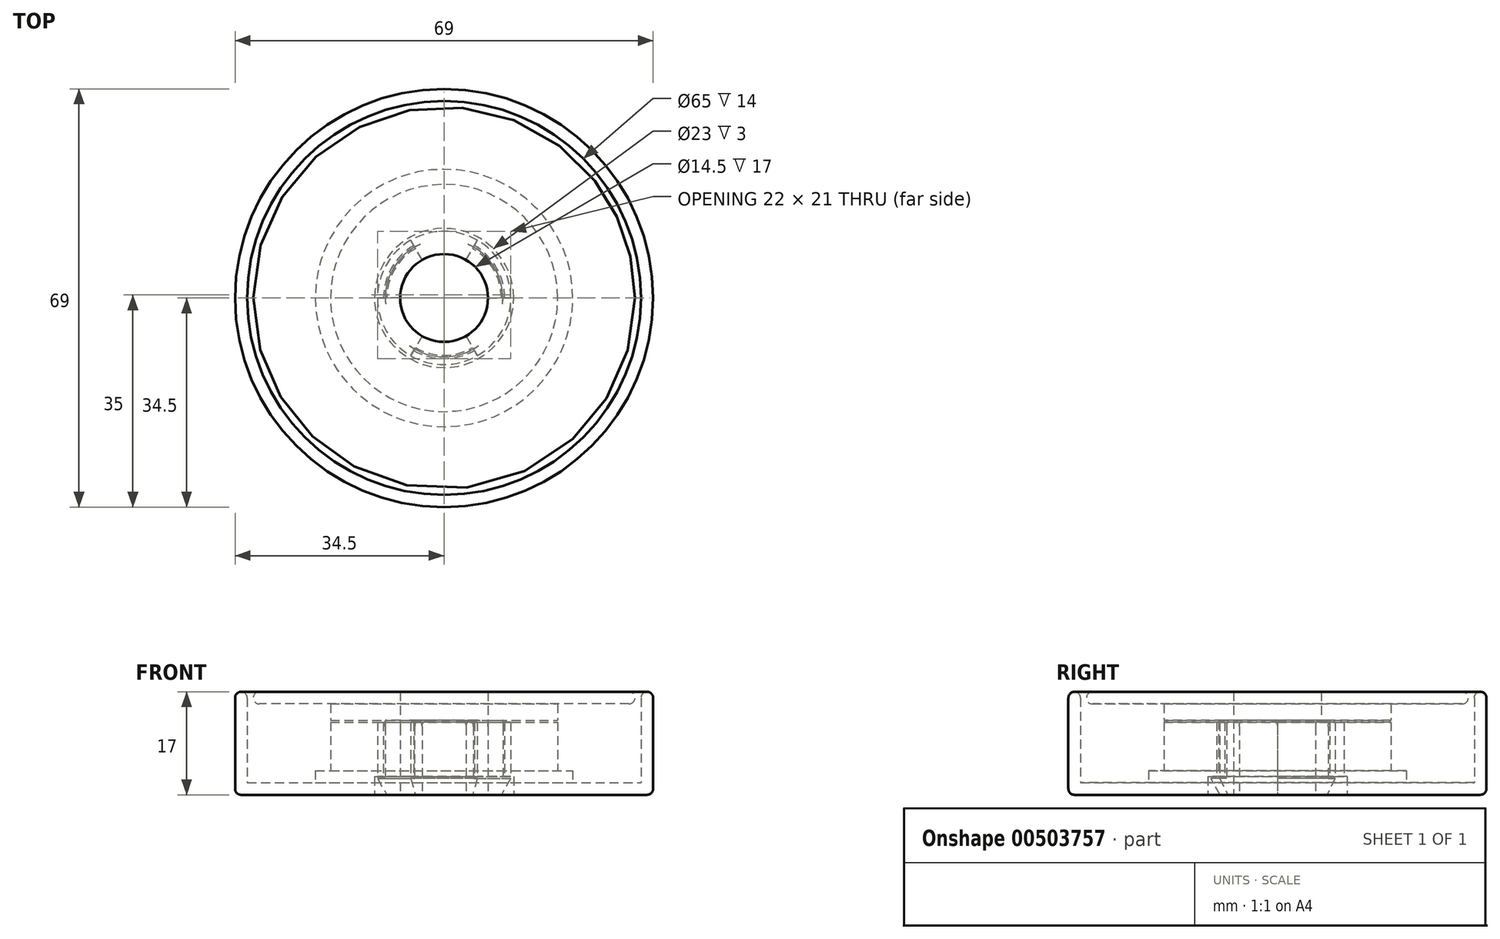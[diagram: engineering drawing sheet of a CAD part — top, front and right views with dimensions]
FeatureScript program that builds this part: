
annotation { "Feature Type Name" : "Feature", "Feature Type Description" : "" }
export const myFeature = defineFeature(function(context is Context, id is Id, definition is map)
    precondition{}
    {
        {
            var Q0;
            Q0=qCreatedBy(makeId("Front.planeOp"),FACE);
            var sketch = newSketch(context, id + "F0", { "sketchPlane" : qUnion([Q0])});
            skLineSegment(sketch, "E0", {"start": v(10, 12) * mm, "end": v(10, 3) * mm});
            skLineSegment(sketch, "E1", {"start": v(11.5, 0) * mm, "end": v(34.5, 0) * mm});
            skLineSegment(sketch, "E2", {"start": v(34.5, 0) * mm, "end": v(34.5, 17) * mm});
            skLineSegment(sketch, "E3", {"start": v(34.5, 17) * mm, "end": v(32.5, 17) * mm});
            skLineSegment(sketch, "E4", {"start": v(32.5, 17) * mm, "end": v(32.5, 2) * mm});
            skLineSegment(sketch, "E5", {"start": v(32.5, 2) * mm, "end": v(21.25, 2) * mm});
            skLineSegment(sketch, "E6", {"start": v(21.25, 2) * mm, "end": v(21.25, 4) * mm});
            skLineSegment(sketch, "E7", {"start": v(21.25, 4) * mm, "end": v(18.75, 4) * mm});
            skLineSegment(sketch, "E8", {"start": v(18.75, 4) * mm, "end": v(18.75, 12) * mm});
            skLineSegment(sketch, "E9", {"start": v(18.75, 12) * mm, "end": v(10, 12) * mm});
            skLineSegment(sketch, "E10", {"start": v(10, 3) * mm, "end": v(11.5, 3) * mm});
            skLineSegment(sketch, "E11", {"start": v(11.5, 3) * mm, "end": v(11.5, 0) * mm});
            skPoint(sketch, "E12.orphan", {"position": v(10, 0) * mm});
            skLineSegment(sketch, "E13", {"start": v(0, 0) * mm, "end": v(0, 12) * mm, "construction": true});
            skLineSegment(sketch, "E14", {"start": v(7.25, 17) * mm, "end": v(31.5, 17) * mm});
            skPoint(sketch, "E14.startSnap0", {"position": v(33.5, 17) * mm});
            skLineSegment(sketch, "E15", {"start": v(31.5, 17) * mm, "end": v(31.5, 15) * mm});
            skLineSegment(sketch, "E16", {"start": v(31.5, 15) * mm, "end": v(18.75, 15) * mm});
            skLineSegment(sketch, "E17", {"start": v(18.75, 15) * mm, "end": v(18.75, 12.3) * mm});
            skLineSegment(sketch, "E18", {"start": v(18.75, 12.3) * mm, "end": v(9.7, 12.3) * mm});
            skLineSegment(sketch, "E19", {"start": v(9.7, 12.3) * mm, "end": v(9.7, 2.7) * mm});
            skLineSegment(sketch, "E20", {"start": v(9.7, 2.7) * mm, "end": v(11, 2.7) * mm});
            skLineSegment(sketch, "E21", {"start": v(11, 2.7) * mm, "end": v(9.44, 0) * mm});
            skLineSegment(sketch, "E22", {"start": v(9.44, 0) * mm, "end": v(7.25, 0) * mm});
            skLineSegment(sketch, "E23", {"start": v(7.25, 0) * mm, "end": v(7.25, 17) * mm});
            skSolve(sketch);
        }
        {
            var Q0;
            Q0 = qSketchRegion(id + "F0", true);
            var Q1;
            Q1=sQuery(id+"F0.wireOp",EDGE,"E13");
            revolve(context, id + "F1", {"entities" : qUnion([Q0]), "axis" : qUnion([Q1]), "revolveType" : RevolveType.FULL});
        }
        {
            var Q0;
            Q0=makeQuery(id+"F1.opRevolve","SWEPT_FACE",FACE,{"disambiguationData":[OSD([sQuery(id+"F0.wireOp",EDGE,"E22")])]});
            var sketch = newSketch(context, id + "F2", { "sketchPlane" : qUnion([Q0])});
            skArc(sketch, "E24", {"start": v(-5.5, -9.53) * mm, "mid": v(0, -11) * mm, "end": v(5.5, -9.53) * mm});
            skLineSegment(sketch, "E25", {"start": v(-3.63, -6.28) * mm, "end": v(-5.5, -9.53) * mm});
            skLineSegment(sketch, "E26", {"start": v(3.63, -6.28) * mm, "end": v(5.5, -9.53) * mm});
            skLineSegment(sketch, "E27", {"start": v(0, 0) * mm, "end": v(11, 0) * mm});
            skLineSegment(sketch, "E28", {"start": v(3.62, 6.28) * mm, "end": v(5.5, 9.53) * mm});
            skArc(sketch, "E29", {"start": v(-3.63, -6.28) * mm, "mid": v(0, -7.25) * mm, "end": v(3.63, -6.28) * mm});
            skLineSegment(sketch, "E30", {"start": v(0, 0) * mm, "end": v(-11, 0) * mm});
            skLineSegment(sketch, "E31", {"start": v(-3.63, 6.28) * mm, "end": v(-5.5, 9.53) * mm});
            skArc(sketch, "E32.trimOffspring", {"start": v(7.25, 0) * mm, "mid": v(6.28, 3.63) * mm, "end": v(3.62, 6.28) * mm});
            skArc(sketch, "E33.trimOffspring", {"start": v(11, 0) * mm, "mid": v(9.53, 5.5) * mm, "end": v(5.5, 9.53) * mm});
            skArc(sketch, "E34.trimOffspring", {"start": v(-3.63, 6.28) * mm, "mid": v(-6.28, 3.63) * mm, "end": v(-7.25, 0) * mm});
            skArc(sketch, "E35.trimOffspring", {"start": v(-5.5, 9.53) * mm, "mid": v(-9.53, 5.5) * mm, "end": v(-11, 0) * mm});
            skSolve(sketch);
        }
        {
            var Q0;
            {var subQ0=sQuery(id+"F2.wireOp",EDGE,"E24");Q0=makeQuery(id+"F2.imprint","IMPRINT",FACE,{"disambiguationData":[TD([[makeQuery(id+"F2.imprint","IMPRINT",EDGE,{"derivedFrom":subQ0}),1.0]])]});}
            var Q1;
            {var subQ0=sQuery(id+"F2.wireOp",EDGE,"E29");Q1=makeQuery(id+"F2.imprint","IMPRINT",FACE,{"disambiguationData":[TD([[makeQuery(id+"F2.imprint","IMPRINT",EDGE,{"derivedFrom":subQ0}),-1.0]])]});}
            var Q2;
            {var subQ0=sQuery(id+"F2.wireOp",EDGE,"E35.trimOffspring");Q2=makeQuery(id+"F2.imprint","IMPRINT",FACE,{"disambiguationData":[TD([[makeQuery(id+"F2.imprint","IMPRINT",EDGE,{"derivedFrom":subQ0}),1.0]])]});}
            var Q3;
            {var subQ0=sQuery(id+"F2.wireOp",EDGE,"E32.trimOffspring");Q3=makeQuery(id+"F2.imprint","IMPRINT",FACE,{"disambiguationData":[TD([[makeQuery(id+"F2.imprint","IMPRINT",EDGE,{"derivedFrom":subQ0}),-1.0]])]});}
            var Q4;
            {var subQ0=sQuery(id+"F2.wireOp",EDGE,"E33.trimOffspring");Q4=makeQuery(id+"F2.imprint","IMPRINT",FACE,{"disambiguationData":[TD([[makeQuery(id+"F2.imprint","IMPRINT",EDGE,{"derivedFrom":subQ0}),1.0]])]});}
            var Q5;
            {var subQ0=sQuery(id+"F2.wireOp",EDGE,"E34.trimOffspring");Q5=makeQuery(id+"F2.imprint","IMPRINT",FACE,{"disambiguationData":[TD([[makeQuery(id+"F2.imprint","IMPRINT",EDGE,{"derivedFrom":subQ0}),-1.0]])]});}
            var Q6;
            Q6=makeQuery(id+"F1.opRevolve","SWEPT_FACE",FACE,{"disambiguationData":[OSD([sQuery(id+"F0.wireOp",EDGE,"E18")])]});
            extrude(context, id + "F3", {"entities" : qUnion([Q0, Q1, Q2, Q3, Q4, Q5]), "operationType" : NewBodyOperationType.REMOVE, "endBound" : BoundingType.UP_TO_SURFACE, "oppositeDirection" : true, "depth" : 25 * mm, "endBoundEntityFace" : qUnion([Q6]), "offsetDistance" : 25 * mm});
        }
        {
            var Q0;
            Q0=makeQuery(id+"F3.boolean.opBoolean","COPY",EDGE,{"derivedFrom":makeQuery(id+"F3.opExtrude","CAP_EDGE",EDGE,{"disambiguationData":[OSD([sQuery(id+"F2.wireOp",EDGE,"E25")])],"isStart":false})});
            var Q1;
            Q1=makeQuery(id+"F3.boolean.opBoolean","COPY",EDGE,{"derivedFrom":makeQuery(id+"F3.opExtrude","CAP_EDGE",EDGE,{"disambiguationData":[OSD([sQuery(id+"F2.wireOp",EDGE,"E26")])],"isStart":false})});
            var Q2;
            Q2=makeQuery(id+"F3.boolean.opBoolean","COPY",EDGE,{"derivedFrom":makeQuery(id+"F3.opExtrude","CAP_EDGE",EDGE,{"disambiguationData":[OSD([sQuery(id+"F2.wireOp",EDGE,"E30")])],"isStart":false})});
            var Q3;
            Q3=makeQuery(id+"F3.boolean.opBoolean","COPY",EDGE,{"derivedFrom":makeQuery(id+"F3.opExtrude","CAP_EDGE",EDGE,{"disambiguationData":[OSD([sQuery(id+"F2.wireOp",EDGE,"E31")])],"isStart":false})});
            var Q4;
            Q4=makeQuery(id+"F3.boolean.opBoolean","COPY",EDGE,{"derivedFrom":makeQuery(id+"F3.opExtrude","CAP_EDGE",EDGE,{"disambiguationData":[OSD([sQuery(id+"F2.wireOp",EDGE,"E28")])],"isStart":false})});
            var Q5;
            Q5=makeQuery(id+"F3.boolean.opBoolean","COPY",EDGE,{"derivedFrom":makeQuery(id+"F3.opExtrude","CAP_EDGE",EDGE,{"disambiguationData":[OSD([sQuery(id+"F2.wireOp",EDGE,"E27")])],"isStart":false})});
            var Q6;
            Q6=makeQuery(id+"F1.opRevolve","SWEPT_EDGE",EDGE,{"disambiguationData":[OSD([sQuery(id+"F0.wireOp",EDGE,"E15"),sQuery(id+"F0.wireOp",EDGE,"E16")])]});
            var Q7;
            Q7=makeQuery(id+"F1.opRevolve","SWEPT_EDGE",EDGE,{"disambiguationData":[OSD([sQuery(id+"F0.wireOp",EDGE,"E14"),sQuery(id+"F0.wireOp",EDGE,"E15")])]});
            fillet(context, id + "F4", {"entities" : qUnion([Q0, Q1, Q2, Q3, Q4, Q5, Q6, Q7]), "radius" : 1 * mm, "tangentPropagation" : true, "allowEdgeOverflow" : false});
        }
        {
            var Q0;
            Q0=makeQuery(id+"F1.opRevolve","SWEPT_EDGE",EDGE,{"disambiguationData":[OSD([sQuery(id+"F0.wireOp",EDGE,"E3"),sQuery(id+"F0.wireOp",EDGE,"E4")])]});
            var Q1;
            Q1=makeQuery(id+"F1.opRevolve","SWEPT_EDGE",EDGE,{"disambiguationData":[OSD([sQuery(id+"F0.wireOp",EDGE,"E2"),sQuery(id+"F0.wireOp",EDGE,"E3")])]});
            var Q2;
            Q2=makeQuery(id+"F1.opRevolve","SWEPT_EDGE",EDGE,{"disambiguationData":[OSD([sQuery(id+"F0.wireOp",EDGE,"E1"),sQuery(id+"F0.wireOp",EDGE,"E2")])]});
            fillet(context, id + "F5", {"entities" : qUnion([Q0, Q1, Q2]), "radius" : 1 * mm, "tangentPropagation" : true, "allowEdgeOverflow" : false});
        }
    });
